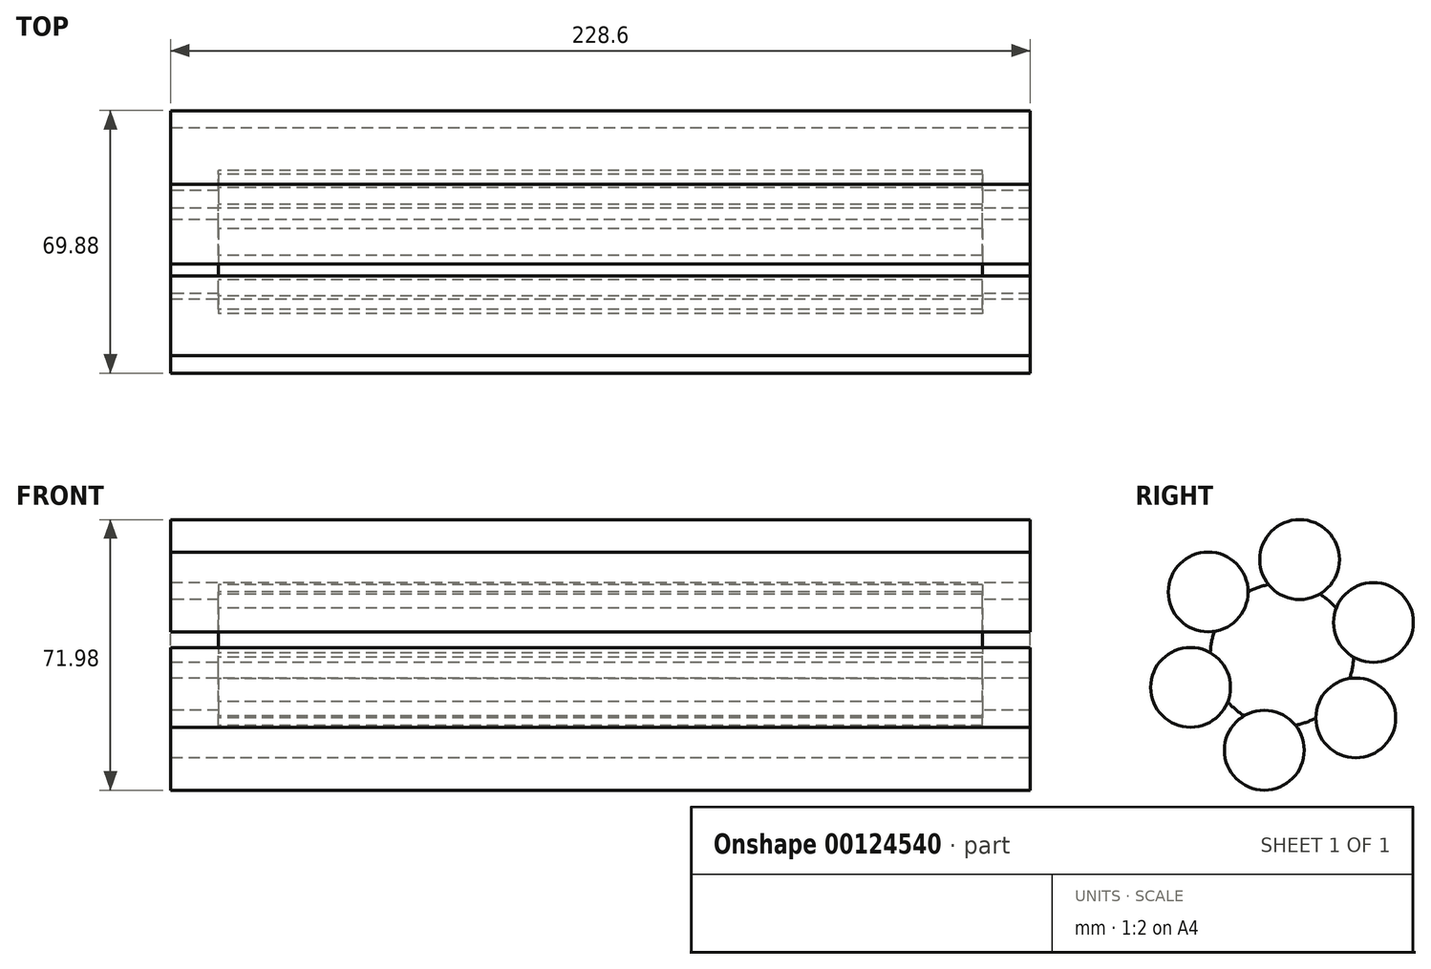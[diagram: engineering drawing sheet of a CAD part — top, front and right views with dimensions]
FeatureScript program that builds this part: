
annotation { "Feature Type Name" : "Feature", "Feature Type Description" : "" }
export const myFeature = defineFeature(function(context is Context, id is Id, definition is map)
    precondition{}
    {
        {
            var Q0;
            Q0=qCreatedBy(makeId("Right.planeOp"),FACE);
            var sketch = newSketch(context, id + "F0", { "sketchPlane" : qUnion([Q0])});
            skCircle(sketch, "E0", {"center": v(0, 0) * mm, "radius": 19.05 * mm});
            skSolve(sketch);
        }
        {
            var Q0;
            Q0=makeQuery(id+"F0.imprint","IMPRINT",FACE,{"disambiguationData":[TD([[makeQuery(id+"F0.imprint","IMPRINT",EDGE,{"derivedFrom":sQuery(id+"F0.wireOp",EDGE,"E0")}),1.0]])]});
            extrude(context, id + "F1", {"entities" : qUnion([Q0]), "endBound" : BoundingType.SYMMETRIC, "depth" : 203.2 * mm});
        }
        {
            var Q0;
            Q0=qCreatedBy(makeId("Right.planeOp"),FACE);
            var sketch = newSketch(context, id + "F2", { "sketchPlane" : qUnion([Q0])});
            skPoint(sketch, "E1", {"position": v(-19.63, 16.75) * mm});
            skCircle(sketch, "E2", {"center": v(-19.63, 16.75) * mm, "radius": 10.61 * mm});
            skCircle(sketch, "E3.1.0", {"center": v(-24.32, -8.62) * mm, "radius": 10.61 * mm});
            skCircle(sketch, "E3.2.0", {"center": v(-4.7, -25.37) * mm, "radius": 10.61 * mm});
            skCircle(sketch, "E3.3.0", {"center": v(19.63, -16.75) * mm, "radius": 10.61 * mm});
            skCircle(sketch, "E3.4.0", {"center": v(24.32, 8.62) * mm, "radius": 10.61 * mm});
            skCircle(sketch, "E3.5.0", {"center": v(4.7, 25.37) * mm, "radius": 10.61 * mm});
            skPoint(sketch, "E3.center", {"position": v(0, 0) * mm});
            skSolve(sketch);
        }
        {
            var Q0;
            Q0=makeQuery(id+"F2.imprint","IMPRINT",FACE,{"disambiguationData":[TD([[makeQuery(id+"F2.imprint","IMPRINT",EDGE,{"derivedFrom":sQuery(id+"F2.wireOp",EDGE,"E2")}),1.0]])]});
            var Q1;
            Q1 = qSketchRegion(id + "F2", true);
            extrude(context, id + "F3", {"entities" : qUnion([Q0, Q1]), "operationType" : NewBodyOperationType.ADD, "endBound" : BoundingType.SYMMETRIC, "depth" : 228.6 * mm});
        }
    });
